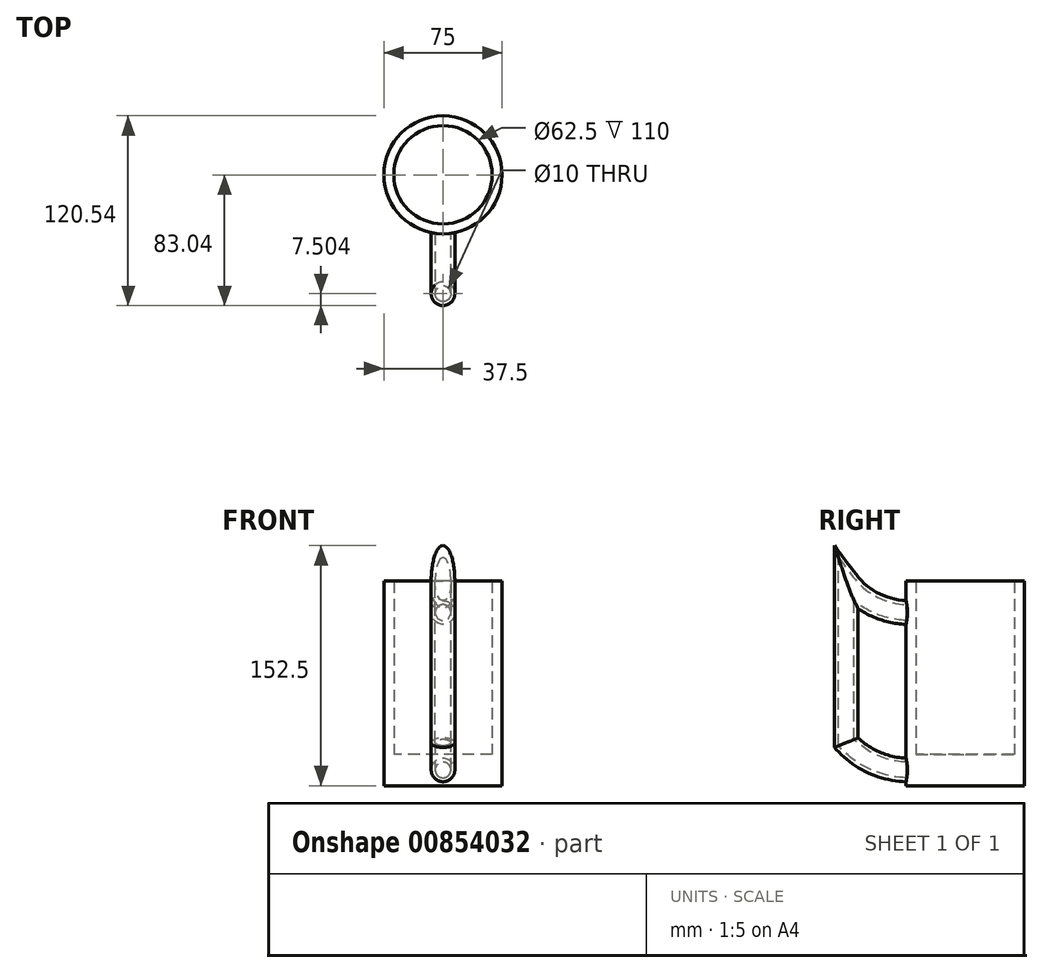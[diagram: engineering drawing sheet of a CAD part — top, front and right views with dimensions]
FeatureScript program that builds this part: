
annotation { "Feature Type Name" : "Feature", "Feature Type Description" : "" }
export const myFeature = defineFeature(function(context is Context, id is Id, definition is map)
    precondition{}
    {
        {
            var Q0;
            Q0=qCreatedBy(makeId("Top.planeOp"),FACE);
            var sketch = newSketch(context, id + "F0", { "sketchPlane" : qUnion([Q0])});
            skCircle(sketch, "E0", {"center": v(0, 0) * mm, "radius": 37.5 * mm});
            skCircle(sketch, "E1", {"center": v(0, 0) * mm, "radius": 31.25 * mm});
            skSolve(sketch);
        }
        {
            var Q0;
            Q0 = qSketchRegion(id + "F0", true);
            extrude(context, id + "F1", {"entities" : qUnion([Q0]), "depth" : 130 * mm, "offsetDistance" : 25 * mm});
        }
        {
            var Q0;
            Q0=makeQuery(id+"F0.imprint","IMPRINT",FACE,{"disambiguationData":[TD([[makeQuery(id+"F0.imprint","IMPRINT",EDGE,{"derivedFrom":sQuery(id+"F0.wireOp",EDGE,"E1")}),1.0]])]});
            extrude(context, id + "F2", {"entities" : qUnion([Q0]), "operationType" : NewBodyOperationType.ADD, "depth" : 20 * mm, "offsetDistance" : 25 * mm});
        }
        {
            var Q0;
            Q0=qCreatedBy(makeId("Right.planeOp"),FACE);
            var sketch = newSketch(context, id + "F3", { "sketchPlane" : qUnion([Q0])});
            skLineSegment(sketch, "E2", {"start": v(0, 0) * mm, "end": v(0, 20) * mm});
            skPoint(sketch, "E3", {"position": v(0, 10) * mm});
            skLineSegment(sketch, "E4", {"start": v(-75.54, 110) * mm, "end": v(-75.54, 130) * mm});
            skArc(sketch, "E5", {"start": v(-75.54, 130) * mm, "mid": v(-57.9, 115.28) * mm, "end": v(-35.54, 110) * mm});
            skArc(sketch, "E6", {"start": v(-35.54, 10) * mm, "mid": v(-57.33, 14.52) * mm, "end": v(-75.54, 27.32) * mm});
            skLineSegment(sketch, "E7", {"start": v(-75.54, 110) * mm, "end": v(-75.54, 27.32) * mm});
            skPoint(sketch, "E8", {"position": v(-34.39, 20) * mm});
            skLineSegment(sketch, "E9", {"start": v(-34.39, 20) * mm, "end": v(-34.39, 10) * mm});
            skLineSegment(sketch, "E10", {"start": v(-34.39, 10) * mm, "end": v(-35.54, 10) * mm});
            skLineSegment(sketch, "E11", {"start": v(-34.39, 20) * mm, "end": v(-34.39, 110) * mm});
            skLineSegment(sketch, "E12", {"start": v(-34.39, 110) * mm, "end": v(-35.54, 110) * mm});
            skLineSegment(sketch, "E13", {"start": v(0, 10) * mm, "end": v(-34.39, 10) * mm});
            skSolve(sketch);
        }
        {
            var Q0;
            Q0=qCreatedBy(makeId("Front.planeOp"),FACE);
            var sketch = newSketch(context, id + "F4", { "sketchPlane" : qUnion([Q0])});
            skCircle(sketch, "E14", {"center": v(0, 10) * mm, "radius": 7.5 * mm});
            skCircle(sketch, "E15", {"center": v(0, 10) * mm, "radius": 5 * mm});
            skSolve(sketch);
        }
        {
            var Q0;
            Q0 = qSketchRegion(id + "F4", true);
            var Q1;
            Q1=sQuery(id+"F3.wireOp",EDGE,"E13");
            var Q2;
            Q2=sQuery(id+"F3.wireOp",EDGE,"E10");
            var Q3;
            Q3=sQuery(id+"F3.wireOp",EDGE,"E6");
            var Q4;
            Q4=sQuery(id+"F3.wireOp",EDGE,"E7");
            var Q5;
            Q5=sQuery(id+"F3.wireOp",EDGE,"E5");
            var Q6;
            Q6=sQuery(id+"F3.wireOp",EDGE,"E4");
            sweep(context, id + "F5", {"operationType" : NewBodyOperationType.ADD, "profiles" : qUnion([Q0]), "path" : qUnion([Q1, Q2, Q3, Q4, Q5, Q6])});
        }
    });
